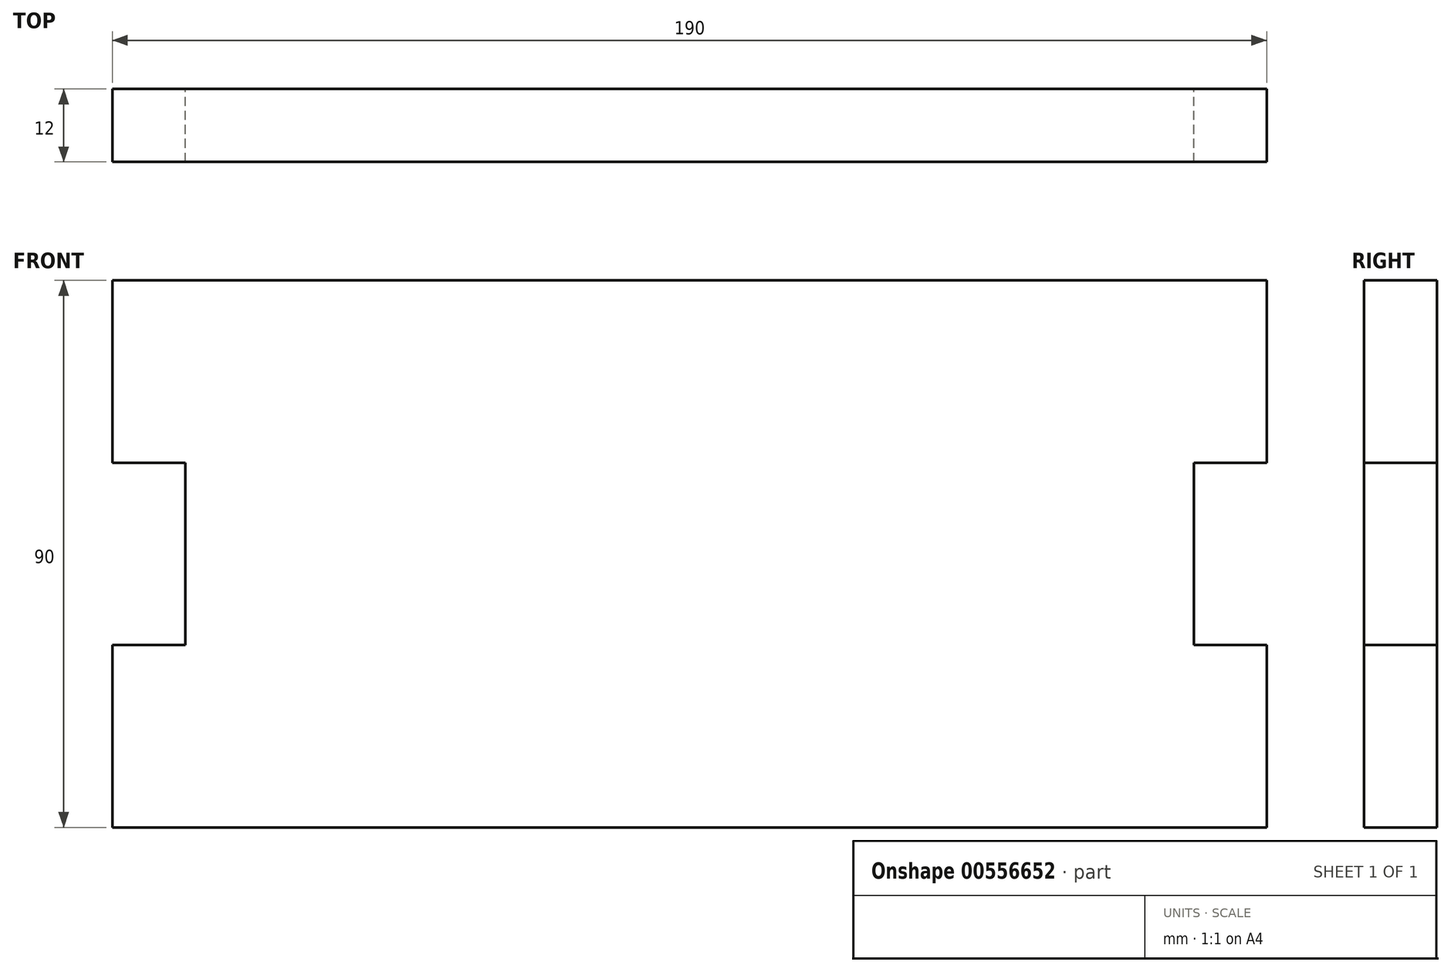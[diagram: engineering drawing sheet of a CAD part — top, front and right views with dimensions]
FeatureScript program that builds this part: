
annotation { "Feature Type Name" : "Feature", "Feature Type Description" : "" }
export const myFeature = defineFeature(function(context is Context, id is Id, definition is map)
    precondition{}
    {
        {
            var Q0;
            Q0=qCreatedBy(makeId("Front.planeOp"),FACE);
            var sketch = newSketch(context, id + "F0", { "sketchPlane" : qUnion([Q0])});
            skLineSegment(sketch, "E0", {"start": v(0, 0) * mm, "end": v(0, 30) * mm});
            skLineSegment(sketch, "E1", {"start": v(0, 30) * mm, "end": v(12, 30) * mm});
            skLineSegment(sketch, "E2", {"start": v(12, 30) * mm, "end": v(12, 60) * mm});
            skLineSegment(sketch, "E3", {"start": v(12, 60) * mm, "end": v(0, 60) * mm});
            skLineSegment(sketch, "E4", {"start": v(0, 60) * mm, "end": v(0, 90) * mm});
            skLineSegment(sketch, "E5", {"start": v(0, 90) * mm, "end": v(95, 90) * mm});
            skLineSegment(sketch, "E6", {"start": v(95, 90) * mm, "end": v(95, 0) * mm, "construction": true});
            skLineSegment(sketch, "E7", {"start": v(0, 0) * mm, "end": v(95, 0) * mm});
            skLineSegment(sketch, "E8.MirrorCS", {"start": v(178, 60) * mm, "end": v(190, 60) * mm});
            skLineSegment(sketch, "E9.MirrorCS", {"start": v(190, 90) * mm, "end": v(95, 90) * mm});
            skLineSegment(sketch, "E10.MirrorCS", {"start": v(190, 0) * mm, "end": v(190, 30) * mm});
            skLineSegment(sketch, "E11.MirrorCS", {"start": v(190, 60) * mm, "end": v(190, 90) * mm});
            skLineSegment(sketch, "E12.MirrorCS", {"start": v(178, 30) * mm, "end": v(178, 60) * mm});
            skLineSegment(sketch, "E13.MirrorCS", {"start": v(190, 30) * mm, "end": v(178, 30) * mm});
            skLineSegment(sketch, "E14.MirrorCS", {"start": v(190, 0) * mm, "end": v(95, 0) * mm});
            skSolve(sketch);
        }
        {
            var Q0;
            Q0 = qSketchRegion(id + "F0", true);
            extrude(context, id + "F1", {"entities" : qUnion([Q0]), "endBound" : BoundingType.SYMMETRIC, "depth" : 12 * mm, "offsetDistance" : 25 * mm});
        }
    });
